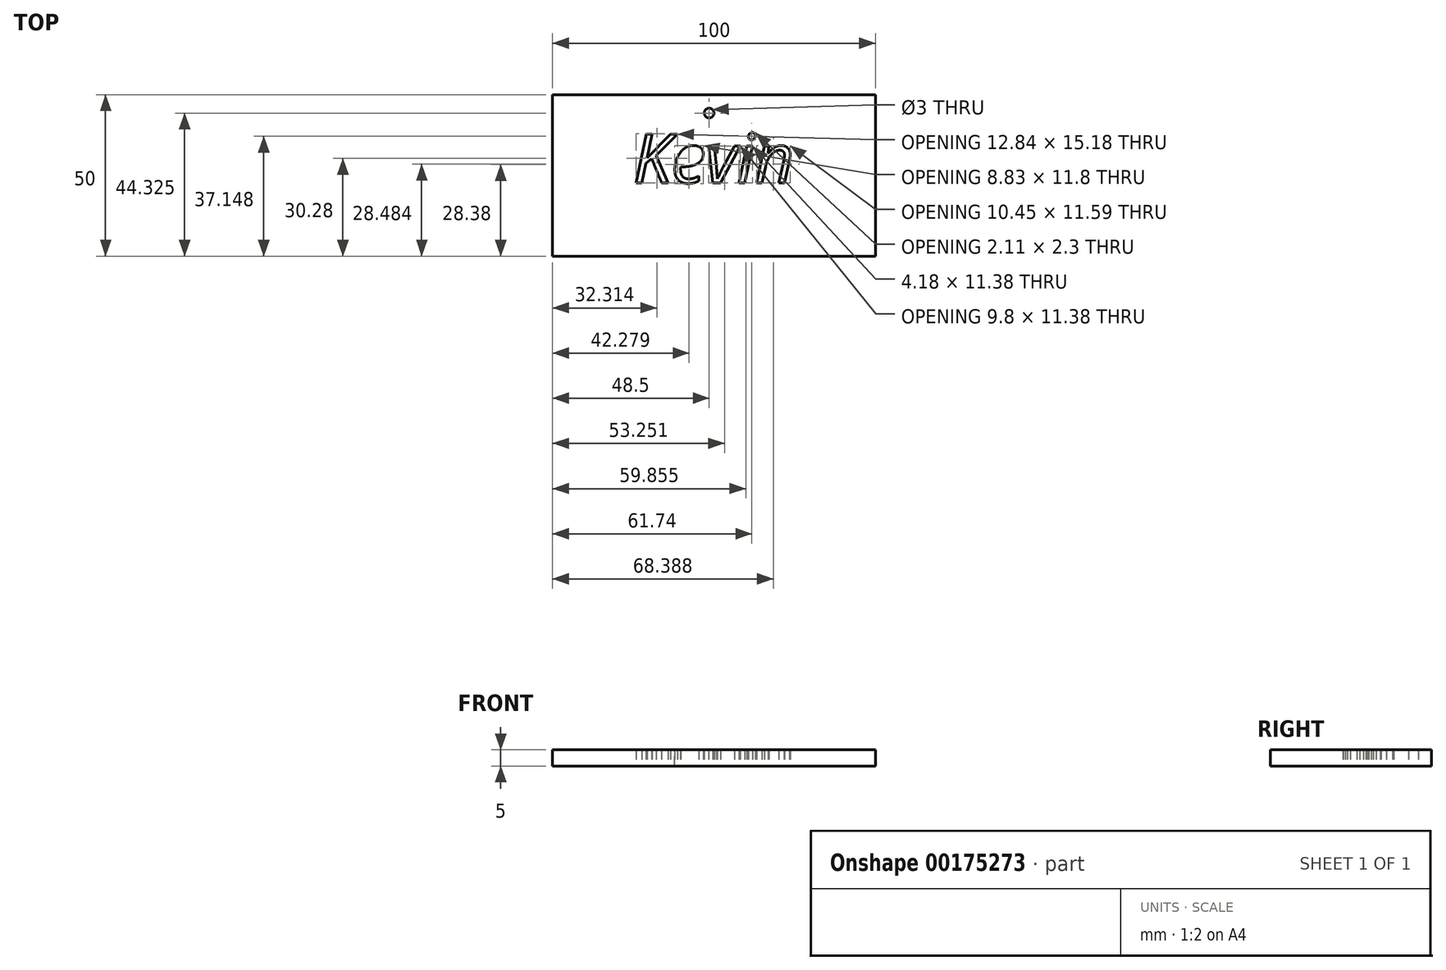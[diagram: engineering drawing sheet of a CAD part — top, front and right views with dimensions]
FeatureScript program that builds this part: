
annotation { "Feature Type Name" : "Feature", "Feature Type Description" : "" }
export const myFeature = defineFeature(function(context is Context, id is Id, definition is map)
    precondition{}
    {
        {
            var Q0;
            Q0=qCreatedBy(makeId("Top.planeOp"),FACE);
            var sketch = newSketch(context, id + "F0", { "sketchPlane" : qUnion([Q0])});
            skLineSegment(sketch, "E0.bottom", {"start": v(-100, 50) * mm, "end": v(0, 50) * mm});
            skLineSegment(sketch, "E0.top", {"start": v(-100, 0) * mm, "end": v(0, 0) * mm});
            skLineSegment(sketch, "E0.left", {"start": v(-100, 50) * mm, "end": v(-100, 0) * mm});
            skLineSegment(sketch, "E0.right", {"start": v(0, 50) * mm, "end": v(0, 0) * mm});
            skText(sketch, "E1", { "text": "Kevin", "fontName": "OpenSans-Italic.ttf"});
            skCircle(sketch, "E2", {"center": v(-51.5, 44.32) * mm, "radius": 1.5 * mm});
            const initialGuessF0  = {"E1": [-0.075, 0.02269, 1, 0, 0.01531]};
            skSetInitialGuess(sketch, initialGuessF0);
            skSolve(sketch);
        }
        {
            var Q0;
            Q0 = qSketchRegion(id + "F0", true);
            extrude(context, id + "F1", {"entities" : qUnion([Q0]), "depth" : 5 * mm});
        }
    });
